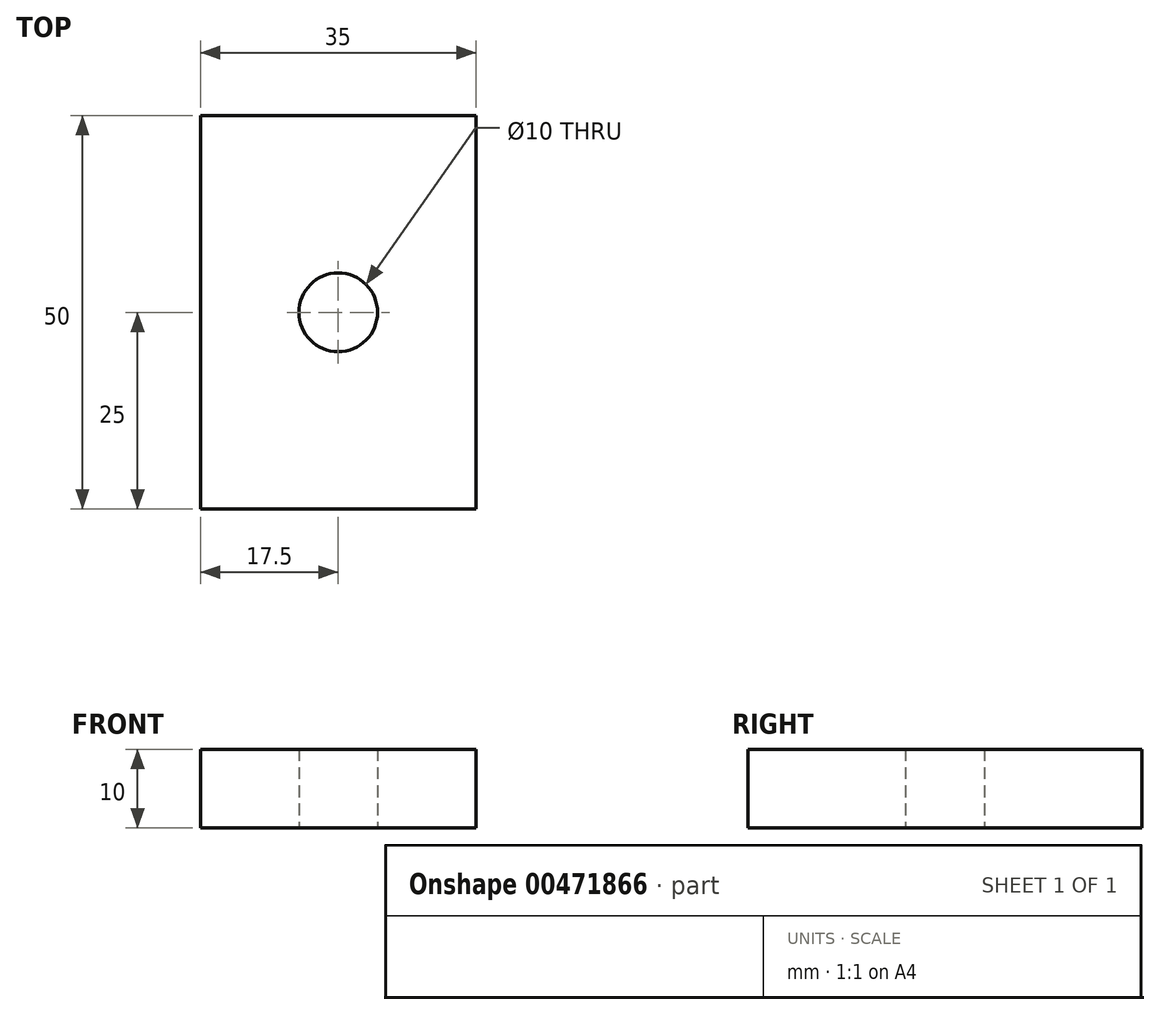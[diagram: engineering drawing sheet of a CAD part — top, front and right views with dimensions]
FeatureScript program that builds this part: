
annotation { "Feature Type Name" : "Feature", "Feature Type Description" : "" }
export const myFeature = defineFeature(function(context is Context, id is Id, definition is map)
    precondition{}
    {
        {
            var Q0;
            Q0=qCreatedBy(makeId("Top.planeOp"),FACE);
            var sketch = newSketch(context, id + "F0", { "sketchPlane" : qUnion([Q0])});
            skLineSegment(sketch, "E0.bottom", {"start": v(0, 0) * mm, "end": v(35, 0) * mm});
            skLineSegment(sketch, "E0.top", {"start": v(0, 50) * mm, "end": v(35, 50) * mm});
            skLineSegment(sketch, "E0.left", {"start": v(0, 0) * mm, "end": v(0, 50) * mm});
            skLineSegment(sketch, "E0.right", {"start": v(35, 0) * mm, "end": v(35, 50) * mm});
            skCircle(sketch, "E1", {"center": v(17.5, 25) * mm, "radius": 5 * mm});
            skSolve(sketch);
        }
        {
            var Q0;
            Q0 = qSketchRegion(id + "F0", true);
            extrude(context, id + "F1", {"entities" : qUnion([Q0]), "depth" : 10 * mm});
        }
    });
